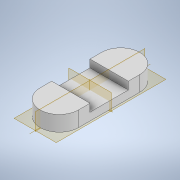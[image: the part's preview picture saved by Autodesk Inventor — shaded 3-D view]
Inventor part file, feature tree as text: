
AUTODESK INVENTOR PART (.ipt)
format: ipt  version: 2022.4 (Build 264492010, 492A)  size: 113,664 bytes
history: native  units: mm
features: extrude x2, sketch x1
ambient origin geometry x8: Origin, YZ Plane, XZ Plane, XY Plane, X Axis, Y Axis, Z Axis, Center Point
bodies: Solid1 (feature_tree)
feature tree (3):
  sketch  "Sketch1"  dims[d0=10.0mm d1=8.0mm d2=3.0mm d3=2.0mm d4=0.0mm d5=4.0mm d6=0.0mm]
  extrude  "Extrusion1"  Depth=8.0mm
  extrude  "Extrusion2"  Depth=4.0mm
